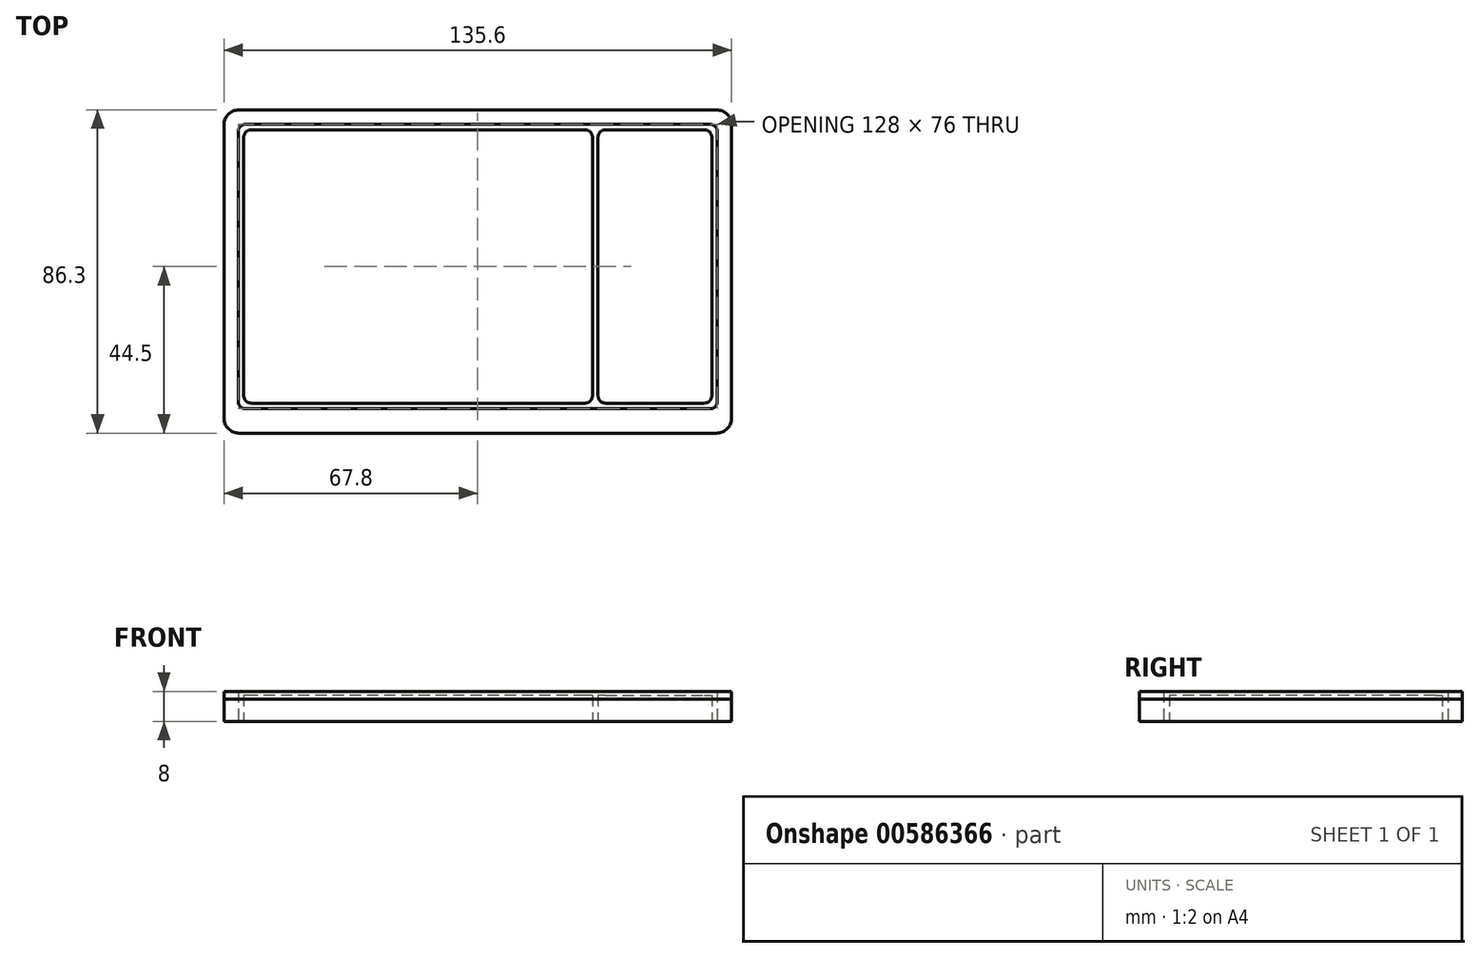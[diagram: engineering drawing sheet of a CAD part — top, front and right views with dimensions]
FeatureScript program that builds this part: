
annotation { "Feature Type Name" : "Feature", "Feature Type Description" : "" }
export const myFeature = defineFeature(function(context is Context, id is Id, definition is map)
    precondition{}
    {
        {
            var Q0;
            Q0=qCreatedBy(makeId("Top.planeOp"),FACE);
            var sketch = newSketch(context, id + "F0", { "sketchPlane" : qUnion([Q0])});
            skLineSegment(sketch, "E0.bottom", {"start": v(77, 39) * mm, "end": v(-47, 39) * mm});
            skLineSegment(sketch, "E0.top", {"start": v(77, -37) * mm, "end": v(-47, -37) * mm});
            skLineSegment(sketch, "E0.left", {"start": v(79, 37) * mm, "end": v(79, -35) * mm});
            skLineSegment(sketch, "E0.right", {"start": v(-49, 37) * mm, "end": v(-49, -35) * mm});
            skPoint(sketch, "E1.visualSharp", {"position": v(79, 39) * mm});
            skArc(sketch, "E1.filletArc", {"start": v(79, 37) * mm, "mid": v(78.41, 38.41) * mm, "end": v(77, 39) * mm});
            skPoint(sketch, "E2.visualSharp", {"position": v(79, -37) * mm});
            skArc(sketch, "E2.filletArc", {"start": v(77, -37) * mm, "mid": v(78.41, -36.41) * mm, "end": v(79, -35) * mm});
            skPoint(sketch, "E3.visualSharp", {"position": v(-49, -37) * mm});
            skArc(sketch, "E3.filletArc", {"start": v(-49, -35) * mm, "mid": v(-48.41, -36.41) * mm, "end": v(-47, -37) * mm});
            skPoint(sketch, "E4.visualSharp", {"position": v(-49, 39) * mm});
            skArc(sketch, "E4.filletArc", {"start": v(-47, 39) * mm, "mid": v(-48.41, 38.41) * mm, "end": v(-49, 37) * mm});
            skLineSegment(sketch, "E5.bottom", {"start": v(-48.8, 42.8) * mm, "end": v(78.8, 42.8) * mm});
            skLineSegment(sketch, "E5.top", {"start": v(-48.8, -43.5) * mm, "end": v(78.8, -43.5) * mm});
            skLineSegment(sketch, "E5.left", {"start": v(-52.8, 38.8) * mm, "end": v(-52.8, -39.5) * mm});
            skLineSegment(sketch, "E5.right", {"start": v(82.8, 38.8) * mm, "end": v(82.8, -39.5) * mm});
            skPoint(sketch, "E6.visualSharp", {"position": v(-52.8, 42.8) * mm});
            skArc(sketch, "E6.filletArc", {"start": v(-48.8, 42.8) * mm, "mid": v(-51.63, 41.63) * mm, "end": v(-52.8, 38.8) * mm});
            skPoint(sketch, "E7.visualSharp", {"position": v(82.8, 42.8) * mm});
            skArc(sketch, "E7.filletArc", {"start": v(82.8, 38.8) * mm, "mid": v(81.63, 41.63) * mm, "end": v(78.8, 42.8) * mm});
            skPoint(sketch, "E8.visualSharp", {"position": v(82.8, -43.5) * mm});
            skArc(sketch, "E8.filletArc", {"start": v(78.8, -43.5) * mm, "mid": v(81.63, -42.33) * mm, "end": v(82.8, -39.5) * mm});
            skPoint(sketch, "E9.visualSharp", {"position": v(-52.8, -43.5) * mm});
            skArc(sketch, "E9.filletArc", {"start": v(-52.8, -39.5) * mm, "mid": v(-51.63, -42.33) * mm, "end": v(-48.8, -43.5) * mm});
            skLineSegment(sketch, "E10.bottom", {"start": v(-45.5, 37.5) * mm, "end": v(75.5, 37.5) * mm});
            skLineSegment(sketch, "E10.top", {"start": v(-45.5, -35.5) * mm, "end": v(75.5, -35.5) * mm});
            skLineSegment(sketch, "E10.left", {"start": v(-47.5, 35.5) * mm, "end": v(-47.5, -33.5) * mm});
            skLineSegment(sketch, "E10.right", {"start": v(77.5, 35.5) * mm, "end": v(77.5, -33.5) * mm});
            skPoint(sketch, "E11.visualSharp", {"position": v(-47.5, 37.5) * mm});
            skArc(sketch, "E11.filletArc", {"start": v(-45.5, 37.5) * mm, "mid": v(-46.91, 36.91) * mm, "end": v(-47.5, 35.5) * mm});
            skPoint(sketch, "E12.visualSharp", {"position": v(77.5, 37.5) * mm});
            skArc(sketch, "E12.filletArc", {"start": v(77.5, 35.5) * mm, "mid": v(76.91, 36.91) * mm, "end": v(75.5, 37.5) * mm});
            skPoint(sketch, "E13.visualSharp", {"position": v(77.5, -35.5) * mm});
            skArc(sketch, "E13.filletArc", {"start": v(75.5, -35.5) * mm, "mid": v(76.91, -34.91) * mm, "end": v(77.5, -33.5) * mm});
            skPoint(sketch, "E14.visualSharp", {"position": v(-47.5, -35.5) * mm});
            skArc(sketch, "E14.filletArc", {"start": v(-47.5, -33.5) * mm, "mid": v(-46.91, -34.91) * mm, "end": v(-45.5, -35.5) * mm});
            skLineSegment(sketch, "E15", {"start": v(47.13, 37.5) * mm, "end": v(47.13, -35.5) * mm});
            skLineSegment(sketch, "E16", {"start": v(45.63, 37.5) * mm, "end": v(45.63, -35.5) * mm});
            skSolve(sketch);
        }
        {
            var Q0;
            Q0=makeQuery(id+"F0.imprint","IMPRINT",FACE,{"disambiguationData":[TD([[makeQuery(id+"F0.imprint","IMPRINT",EDGE,{"derivedFrom":sQuery(id+"F0.wireOp",EDGE,"E0.bottom")}),-1.0]])]});
            extrude(context, id + "F1", {"entities" : qUnion([Q0]), "depth" : 8 * mm, "offsetDistance" : 25 * mm});
        }
        {
            var Q0;
            Q0=qCreatedBy(makeId("Top.planeOp"),FACE);
            var sketch = newSketch(context, id + "F2", { "sketchPlane" : qUnion([Q0])});
            skLineSegment(sketch, "E17.bottom", {"start": v(43.63, 37.5) * mm, "end": v(-45.5, 37.5) * mm});
            skLineSegment(sketch, "E17.top", {"start": v(43.63, -35.5) * mm, "end": v(-45.5, -35.5) * mm});
            skLineSegment(sketch, "E17.left", {"start": v(45.63, 35.5) * mm, "end": v(45.63, -33.5) * mm});
            skLineSegment(sketch, "E17.right", {"start": v(-47.5, 35.5) * mm, "end": v(-47.5, -33.5) * mm});
            skPoint(sketch, "E18.visualSharp", {"position": v(-47.5, 37.5) * mm});
            skArc(sketch, "E18.filletArc", {"start": v(-45.5, 37.5) * mm, "mid": v(-46.91, 36.91) * mm, "end": v(-47.5, 35.5) * mm});
            skPoint(sketch, "E19.visualSharp", {"position": v(45.63, 37.5) * mm});
            skArc(sketch, "E19.filletArc", {"start": v(45.63, 35.5) * mm, "mid": v(45.04, 36.91) * mm, "end": v(43.63, 37.5) * mm});
            skPoint(sketch, "E20.visualSharp", {"position": v(45.63, -35.5) * mm});
            skArc(sketch, "E20.filletArc", {"start": v(43.63, -35.5) * mm, "mid": v(45.04, -34.91) * mm, "end": v(45.63, -33.5) * mm});
            skPoint(sketch, "E21.visualSharp", {"position": v(-47.5, -35.5) * mm});
            skArc(sketch, "E21.filletArc", {"start": v(-47.5, -33.5) * mm, "mid": v(-46.91, -34.91) * mm, "end": v(-45.5, -35.5) * mm});
            skLineSegment(sketch, "E22.bottom", {"start": v(49.13, 37.5) * mm, "end": v(75.5, 37.5) * mm});
            skLineSegment(sketch, "E22.top", {"start": v(49.13, -35.5) * mm, "end": v(75.5, -35.5) * mm});
            skLineSegment(sketch, "E22.left", {"start": v(47.13, 35.5) * mm, "end": v(47.13, -33.5) * mm});
            skLineSegment(sketch, "E22.right", {"start": v(77.5, 35.5) * mm, "end": v(77.5, -33.5) * mm});
            skPoint(sketch, "E23.visualSharp", {"position": v(47.13, 37.5) * mm});
            skArc(sketch, "E23.filletArc", {"start": v(49.13, 37.5) * mm, "mid": v(47.71, 36.91) * mm, "end": v(47.13, 35.5) * mm});
            skPoint(sketch, "E24.visualSharp", {"position": v(77.5, 37.5) * mm});
            skArc(sketch, "E24.filletArc", {"start": v(77.5, 35.5) * mm, "mid": v(76.91, 36.91) * mm, "end": v(75.5, 37.5) * mm});
            skPoint(sketch, "E25.visualSharp", {"position": v(47.13, -35.5) * mm});
            skArc(sketch, "E25.filletArc", {"start": v(47.13, -33.5) * mm, "mid": v(47.71, -34.91) * mm, "end": v(49.13, -35.5) * mm});
            skPoint(sketch, "E26.visualSharp", {"position": v(77.5, -35.5) * mm});
            skArc(sketch, "E26.filletArc", {"start": v(75.5, -35.5) * mm, "mid": v(76.91, -34.91) * mm, "end": v(77.5, -33.5) * mm});
            skSolve(sketch);
        }
        {
            var Q0;
            Q0 = qSketchRegion(id + "F2", true);
            extrude(context, id + "F3", {"entities" : qUnion([Q0]), "operationType" : NewBodyOperationType.ADD, "depth" : 7 * mm, "offsetDistance" : 25 * mm});
        }
        {
            var Q0;
            Q0=qCreatedBy(makeId("Top.planeOp"),FACE);
            var sketch = newSketch(context, id + "F4", { "sketchPlane" : qUnion([Q0])});
            skLineSegment(sketch, "E27.bottom", {"start": v(-48.8, 42.8) * mm, "end": v(78.8, 42.8) * mm});
            skLineSegment(sketch, "E27.top", {"start": v(-48.8, -43.5) * mm, "end": v(78.8, -43.5) * mm});
            skLineSegment(sketch, "E27.left", {"start": v(-52.8, 38.8) * mm, "end": v(-52.8, -39.5) * mm});
            skLineSegment(sketch, "E27.right", {"start": v(82.8, 38.8) * mm, "end": v(82.8, -39.5) * mm});
            skPoint(sketch, "E28.visualSharp", {"position": v(82.8, -43.5) * mm});
            skArc(sketch, "E28.filletArc", {"start": v(78.8, -43.5) * mm, "mid": v(81.63, -42.33) * mm, "end": v(82.8, -39.5) * mm});
            skPoint(sketch, "E29.visualSharp", {"position": v(82.8, 42.8) * mm});
            skArc(sketch, "E29.filletArc", {"start": v(82.8, 38.8) * mm, "mid": v(81.63, 41.63) * mm, "end": v(78.8, 42.8) * mm});
            skPoint(sketch, "E30.visualSharp", {"position": v(-52.8, 42.8) * mm});
            skArc(sketch, "E30.filletArc", {"start": v(-48.8, 42.8) * mm, "mid": v(-51.63, 41.63) * mm, "end": v(-52.8, 38.8) * mm});
            skPoint(sketch, "E31.visualSharp", {"position": v(-52.8, -43.5) * mm});
            skArc(sketch, "E31.filletArc", {"start": v(-52.8, -39.5) * mm, "mid": v(-51.63, -42.33) * mm, "end": v(-48.8, -43.5) * mm});
            skSolve(sketch);
        }
        {
            var Q0;
            Q0 = qSketchRegion(id + "F4", true);
            extrude(context, id + "F5", {"entities" : qUnion([Q0]), "depth" : 6 * mm, "offsetDistance" : 25 * mm});
        }
    });
